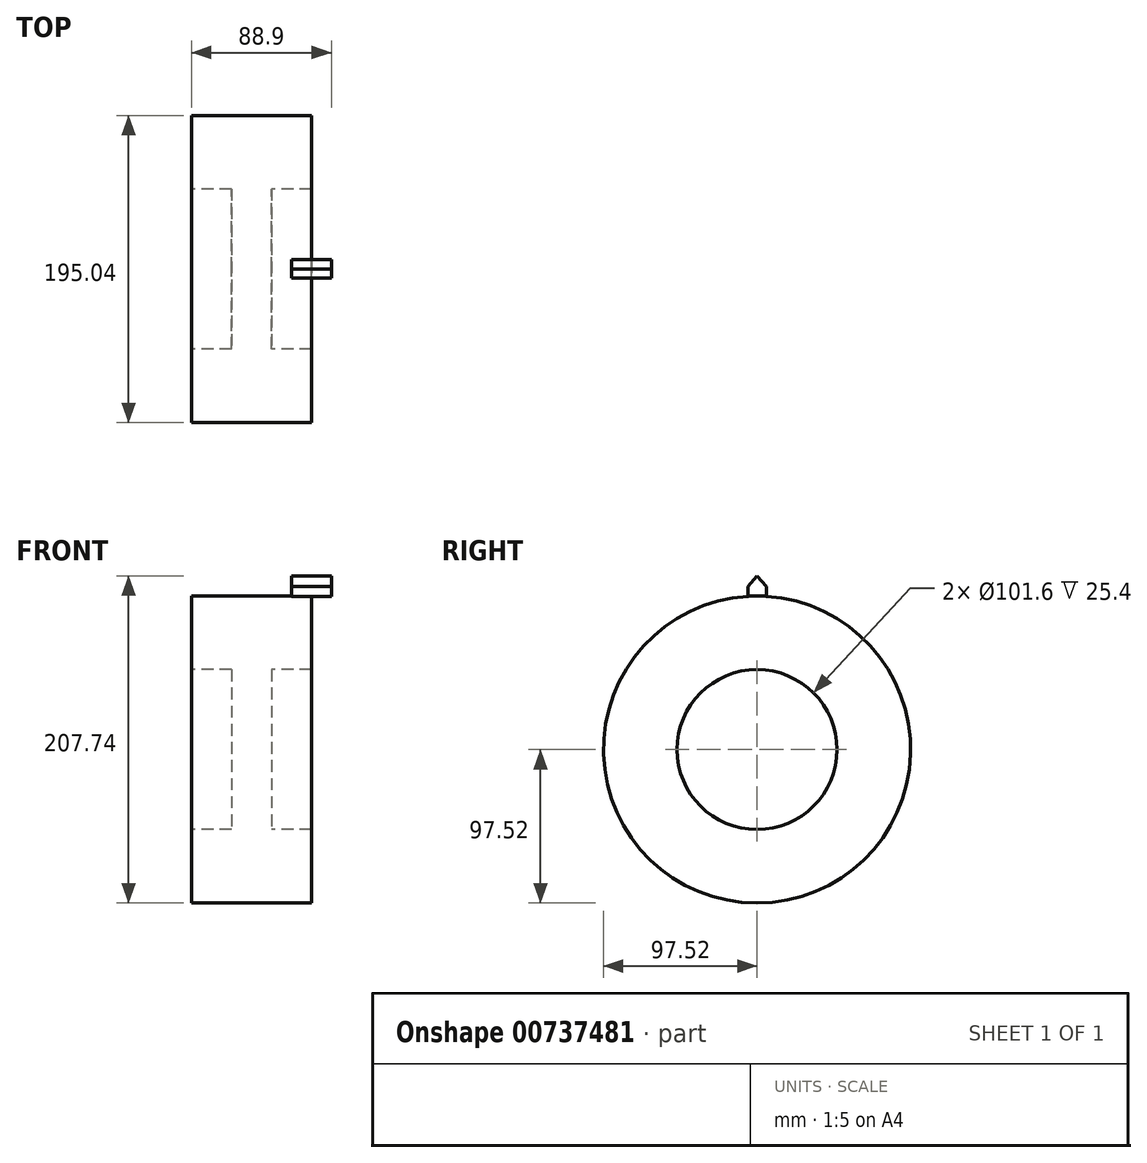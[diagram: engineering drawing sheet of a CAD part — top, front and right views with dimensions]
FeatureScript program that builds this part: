
annotation { "Feature Type Name" : "Feature", "Feature Type Description" : "" }
export const myFeature = defineFeature(function(context is Context, id is Id, definition is map)
    precondition{}
    {
        {
            var Q0;
            Q0=qCreatedBy(makeId("Top.planeOp"),FACE);
            var sketch = newSketch(context, id + "F0", { "sketchPlane" : qUnion([Q0])});
            skLineSegment(sketch, "E0", {"start": v(-159.74, 0) * mm, "end": v(153.45, 0) * mm, "construction": true});
            skLineSegment(sketch, "E1", {"start": v(0, 132.48) * mm, "end": v(0, 0) * mm, "construction": true});
            skLineSegment(sketch, "E2", {"start": v(-38.1, 50.8) * mm, "end": v(-38.1, 97.52) * mm});
            skLineSegment(sketch, "E3.MirrorCS", {"start": v(38.1, 50.8) * mm, "end": v(38.1, 97.52) * mm});
            skLineSegment(sketch, "E4", {"start": v(-38.1, 50.8) * mm, "end": v(-12.7, 50.8) * mm});
            skLineSegment(sketch, "E5", {"start": v(-38.1, 97.52) * mm, "end": v(38.1, 97.52) * mm});
            skLineSegment(sketch, "E6.MirrorCS", {"start": v(38.1, 50.8) * mm, "end": v(12.7, 50.8) * mm});
            skLineSegment(sketch, "E7", {"start": v(-12.7, 50.8) * mm, "end": v(-12.7, 0) * mm});
            skLineSegment(sketch, "E8.MirrorCS", {"start": v(12.7, 50.8) * mm, "end": v(12.7, 0) * mm});
            skLineSegment(sketch, "E9", {"start": v(-12.7, 0) * mm, "end": v(12.7, 0) * mm});
            skSolve(sketch);
        }
        {
            var Q0;
            Q0=makeQuery(id+"F0.imprint","IMPRINT",FACE,{"disambiguationData":[TD([[makeQuery(id+"F0.imprint","IMPRINT",EDGE,{"derivedFrom":sQuery(id+"F0.wireOp",EDGE,"E2")}),-1.0]])]});
            var Q1;
            Q1=sQuery(id+"F0.wireOp",EDGE,"E0");
            revolve(context, id + "F1", {"surfaceOperationType" : NewSurfaceOperationType.NEW, "entities" : qUnion([Q0]), "axis" : qUnion([Q1]), "revolveType" : RevolveType.FULL});
        }
        {
            var Q0;
            Q0=makeQuery(id+"F1.opRevolve","SWEPT_FACE",FACE,{"disambiguationData":[OSD([sQuery(id+"F0.wireOp",EDGE,"E3.MirrorCS")])]});
            var sketch = newSketch(context, id + "F2", { "sketchPlane" : qUnion([Q0])});
            skLineSegment(sketch, "E10", {"start": v(0, 0) * mm, "end": v(0, 97.52) * mm, "construction": true});
            skCircle(sketch, "E11", {"center": v(0, 0) * mm, "radius": 85.5 * mm, "construction": true});
            skLineSegment(sketch, "E12", {"start": v(0, 97.52) * mm, "end": v(0, 121.32) * mm, "construction": true});
            skCircle(sketch, "E13", {"center": v(0, 0) * mm, "radius": 103.87 * mm, "construction": true});
            skCircle(sketch, "E14", {"center": v(0, 0) * mm, "radius": 110.22 * mm, "construction": true});
            skLineSegment(sketch, "E15", {"start": v(-5.85, 97.35) * mm, "end": v(-5.85, 103.7) * mm});
            skLineSegment(sketch, "E16", {"start": v(-5.85, 103.7) * mm, "end": v(0, 110.22) * mm});
            skLineSegment(sketch, "E17.MirrorCS", {"start": v(5.85, 103.7) * mm, "end": v(0, 110.22) * mm});
            skLineSegment(sketch, "E18.MirrorCS", {"start": v(5.85, 97.35) * mm, "end": v(5.85, 103.7) * mm});
            skSolve(sketch);
        }
        {
            var Q0;
            {var subQ1=sQuery(id+"F2.wireOp",EDGE,"E15");Q0=makeQuery(id+"F2.imprint","IMPRINT",FACE,{"disambiguationData":[TD([[makeQuery(id+"F2.imprint","IMPRINT",EDGE,{"derivedFrom":subQ1}),-1.0]])]});}
            extrude(context, id + "F3", {"entities" : qUnion([Q0]), "operationType" : NewBodyOperationType.ADD, "endBound" : BoundingType.SYMMETRIC, "depth" : 25.4 * mm, "offsetDistance" : 25.4 * mm});
        }
    });
